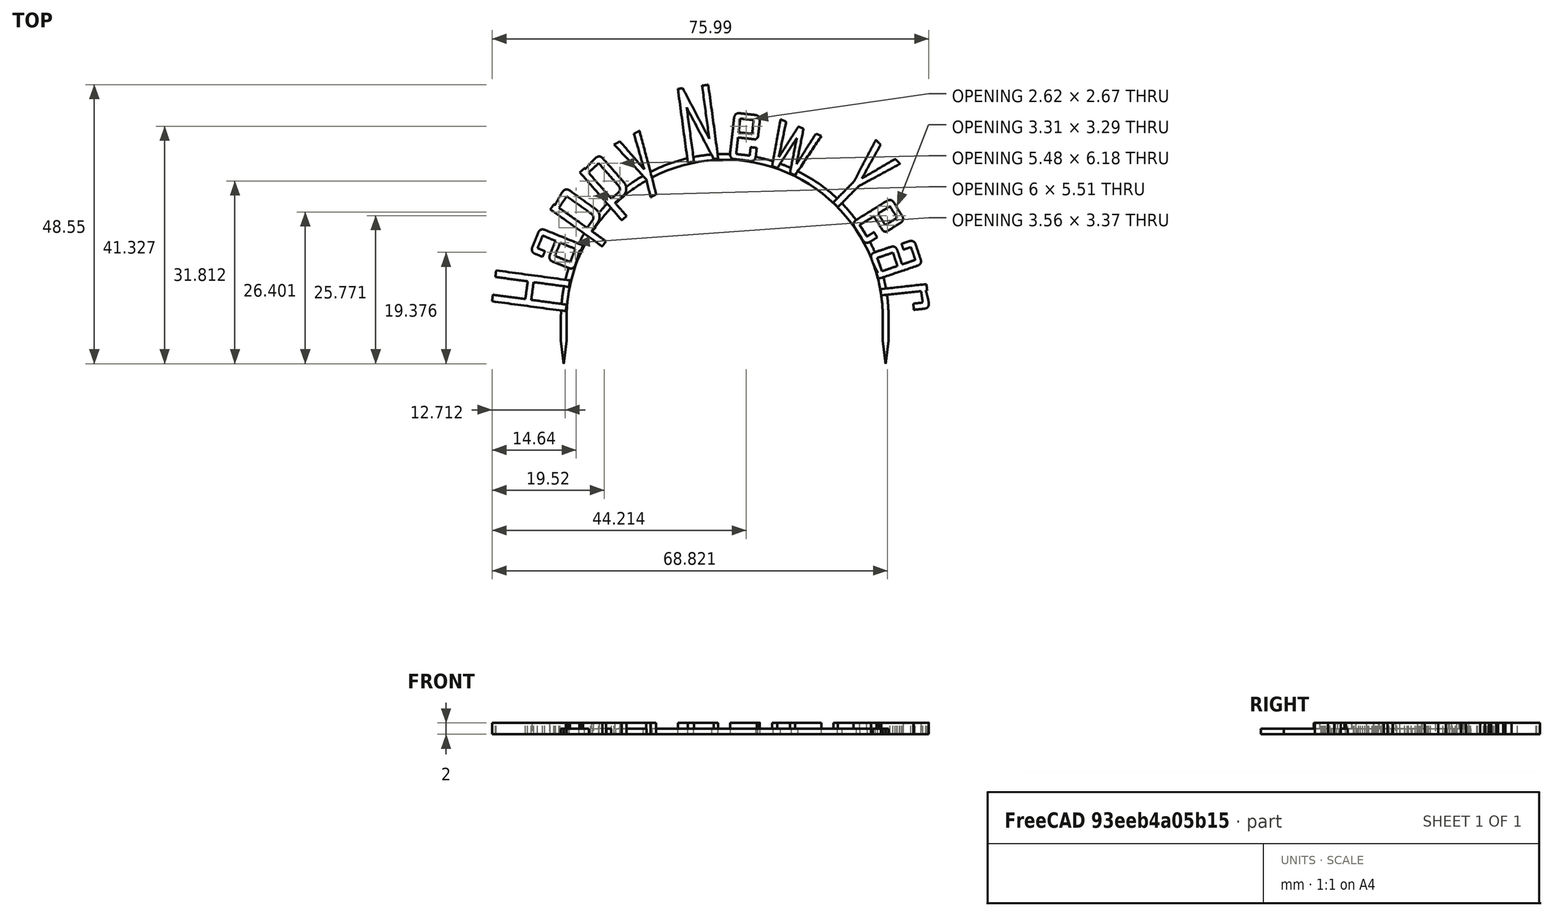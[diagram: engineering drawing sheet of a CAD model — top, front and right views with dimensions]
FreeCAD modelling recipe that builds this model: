
FCSTD DOCUMENT  (FreeCAD 0.20R29177 (Git))
Label: cake-topper-halloween
License: All rights reserved
LicenseURL: http://en.wikipedia.org/wiki/All_rights_reserved
objects: Part::Feature×18, Sketcher::SketchObject×4, PartDesign::Pad×4, App::DocumentObjectGroup×3, App::TextDocument×1, Spreadsheet::Sheet×1, PartDesign::Plane×1, PartDesign::Body×1, Mesh::Feature×1
note: 32 computed .brp shape members not serialized (recipe doc carries the construction recipe); baked Part::Feature solids carry a one-line shape summary decoded from their .brp

FEATURE [App::TextDocument] Text_document  label="Text document"
FEATURE [Spreadsheet::Sheet] Spreadsheet
  cells = A1=Text height; B1=text_h; C1(dim_text_h)==2mm; A2=Text offset x; B2=text_x; C2(dim_text_x)==-105.3mm; A3=Text offset y; B3=text_y; C3(dim_text_y)==177.4mm; A4=Scaffold height; B4=scaffold_h; C4(dim_scaffold_h)==1mm; A5=Scaffold width; B5=scaffold_w; C5(dim_scaffold_w)==1mm; A6=Scaffold inner radius; B6=scaffold_ir; C6(dim_scaffold_ir)==27.5mm; A7=Scaffold outer radius; B7=scaffold_or; C7(dim_scaffold_or)==dim_scaffold_ir + dim_scaffold_w; A8=Tines length; B8=tine_l; C8(dim_tine_l)==4mm; A9=Tines shaft length; B9=tine_shaft_l; C9(dim_tine_shaft_l)==4mm
FEATURE [PartDesign::Plane] DatumPlane  label="BaseXYDatumPlane"
  Length = 90.097
  MapMode = 5
  ResizeMode = 0
  Support = -> [XY_Plane]
  Width = 79.6672
FEATURE [Sketcher::SketchObject] Sketch001  label="ArcSketch"
  FullyConstrained = true
  MapMode = 5
  Support = -> [DatumPlane]
  expr: Constraints[15] = Spreadsheet.dim_scaffold_or
  expr: Constraints[37] = Spreadsheet.dim_tine_shaft_l
  expr: Constraints[38] = Spreadsheet.dim_tine_l
  expr: Constraints[59] = Spreadsheet.dim_scaffold_or
  expr: Constraints[6] = Spreadsheet.dim_scaffold_ir
  sketch-geometry (35):
    g0: ArcOfCircle CenterX=0 CenterY=0 CenterZ=0 NormalX=0 NormalY=0 NormalZ=1 AngleXU=0 Radius=27.5 StartAngle=0 EndAngle=3.14159
    g1: LineSegment StartX=-28.5 StartY=0 StartZ=0 EndX=-27.5 EndY=3.4e-15 EndZ=0
    g2: LineSegment StartX=27.5 StartY=0 StartZ=0 EndX=28.5 EndY=0 EndZ=0
    g3: ArcOfCircle CenterX=0 CenterY=0 CenterZ=0 NormalX=0 NormalY=0 NormalZ=1 AngleXU=0 Radius=28.5 StartAngle=0 EndAngle=0.185163
    g4: ArcOfCircle CenterX=0 CenterY=0 CenterZ=0 NormalX=0 NormalY=0 NormalZ=1 AngleXU=0 Radius=28.5 StartAngle=0.185163 EndAngle=0.207269
    g5: LineSegment StartX=27.89 StartY=5.86497 StartZ=0 EndX=33.2988 EndY=6.91633 EndZ=0
    g6: LineSegment StartX=28.0128 StartY=5.24706 StartZ=0 EndX=33.419 EndY=6.2979 EndZ=0
    g7: LineSegment StartX=33.2988 StartY=6.91633 StartZ=0 EndX=33.419 EndY=6.2979 EndZ=0
    g8: LineSegment StartX=-28.5 StartY=0 StartZ=0 EndX=-28.5 EndY=-4 EndZ=0
    g9: LineSegment StartX=-27.5 StartY=3.4e-15 StartZ=0 EndX=-27.5 EndY=-4 EndZ=0
    g10: LineSegment StartX=-28.5 StartY=-4 StartZ=0 EndX=-28 EndY=-8 EndZ=0
    g11: LineSegment StartX=-27.5 StartY=-4 StartZ=0 EndX=-28 EndY=-8 EndZ=0
    g12: LineSegment StartX=-28.5 StartY=-4 StartZ=0 EndX=-28 EndY=-4 EndZ=0
    g13: LineSegment StartX=-28 StartY=-4 StartZ=0 EndX=-27.5 EndY=-4 EndZ=0
    g14: LineSegment StartX=-28 StartY=-4 StartZ=0 EndX=-28 EndY=-8 EndZ=0
    g15: LineSegment StartX=27.5 StartY=-4 StartZ=0 EndX=28 EndY=-4 EndZ=0
    g16: LineSegment StartX=28 StartY=-4 StartZ=0 EndX=28.5 EndY=-4 EndZ=0
    g17: LineSegment StartX=28 StartY=-4 StartZ=0 EndX=28 EndY=-8 EndZ=0
    g18: LineSegment StartX=27.5 StartY=0 StartZ=0 EndX=27.5 EndY=-4 EndZ=0
    g19: LineSegment StartX=28.5 StartY=0 StartZ=0 EndX=28.5 EndY=-4 EndZ=0
    g20: LineSegment StartX=27.5 StartY=-4 StartZ=0 EndX=28 EndY=-8 EndZ=0
    g21: LineSegment StartX=28.5 StartY=-4 StartZ=0 EndX=28 EndY=-8 EndZ=0
    g22: LineSegment StartX=28.5 StartY=0 StartZ=0 EndX=28.5 EndY=28.5 EndZ=0
    g23: LineSegment StartX=27.89 StartY=5.86497 StartZ=0 EndX=0 EndY=5.86497 EndZ=0
    g24: ArcOfCircle CenterX=0 CenterY=0 CenterZ=0 NormalX=0 NormalY=0 NormalZ=1 AngleXU=0 Radius=28.5 StartAngle=2.19288 EndAngle=3.14159
    g25: ArcOfCircle CenterX=0 CenterY=0 CenterZ=0 NormalX=0 NormalY=0 NormalZ=1 AngleXU=0 Radius=28.5 StartAngle=0.207269 EndAngle=2.17112
    g26: ArcOfCircle CenterX=0 CenterY=0 CenterZ=0 NormalX=0 NormalY=0 NormalZ=1 AngleXU=0 Radius=28.5 StartAngle=2.17112 EndAngle=2.19288
    g27: LineSegment StartX=-16.6078 StartY=23.161 StartZ=0 EndX=-19.8518 EndY=27.7734 EndZ=0
    g28: LineSegment StartX=-16.1 StartY=23.5168 StartZ=0 EndX=-19.3446 EndY=28.13 EndZ=0
    g29: LineSegment StartX=-19.8518 StartY=27.7734 StartZ=0 EndX=-19.3446 EndY=28.13 EndZ=0
    g30: LineSegment StartX=-16.1 StartY=23.5168 StartZ=0 EndX=0 EndY=23.5168 EndZ=0
    g31: LineSegment StartX=28.5 StartY=28.5 StartZ=0 EndX=0 EndY=28.5 EndZ=0
    g32: LineSegment StartX=0 StartY=28.5 StartZ=0 EndX=-28.5 EndY=28.5 EndZ=0
    g33: LineSegment StartX=-28.5 StartY=0 StartZ=0 EndX=-28.5 EndY=28.5 EndZ=0
    g34: LineSegment StartX=-19.8518 StartY=28.5 StartZ=0 EndX=-19.8518 EndY=27.7734 EndZ=0
  constraints (96):
    c: Coincident(g0,g-1)
    c: PointOnObject(g0,g-1)
    c: PointOnObject(g0,g-1)
    c: Coincident(g3,g0)
    c: PointOnObject(g24,g-1)
    c: PointOnObject(g3,g-1)
    c: Radius(g0) = 27.5
    c: Coincident(g1,g24)
    c: Coincident(g1,g0)
    c: Coincident(g2,g0)
    c: Coincident(g2,g3)
    c: Coincident(g4,g25)
    c: Coincident(g3,g25)
    c: Coincident(g3,g4)
    c: Coincident(g3,g4)
    c: Radius(g3) = 28.5
    c: Coincident(g5,g25)
    c: Coincident(g6,g3)
    c: Coincident(g7,g5)
    c: Parallel(g5,g6)
    c: Perpendicular(g7,g5)
    c: Coincident(g8,g24)
    c: Vertical(g8)
    c: Coincident(g9,g0)
    c: Vertical(g9)
    c: Coincident(g10,g8)
    c: Coincident(g11,g9)
    c: Coincident(g11,g10)
    c: Coincident(g12,g8)
    c: Horizontal(g12)
    c: Coincident(g13,g12)
    c: Coincident(g13,g9)
    c: Horizontal(g13)
    c: Coincident(g14,g12)
    c: Coincident(g14,g10)
    c: Equal(g13,g12)
    c: Vertical(g14)
    c: DistanceY(g9,g9) = 4
    c: DistanceY(g10,g9) = 4
    c: Horizontal(g15)
    c: Coincident(g16,g15)
    c: Horizontal(g16)
    c: Coincident(g17,g15)
    c: Vertical(g17)
    c: Coincident(g18,g0)
    c: Coincident(g18,g15)
    c: Vertical(g18)
    c: Coincident(g19,g3)
    c: Coincident(g19,g16)
    c: Vertical(g19)
    c: Coincident(g20,g18)
    c: Coincident(g20,g17)
    c: Coincident(g21,g19)
    c: Coincident(g21,g20)
    c: Equal(g18,g9)
    c: Equal(g17,g14)
    c: Equal(g16,g15)
    c: Coincident(g22,g3)
    c: Vertical(g22)
    c: DistanceY(g22,g22) = 28.5
    c: Coincident(g7,g6)
    c: Coincident(g23,g25)
    c: PointOnObject(g23,g-2)
    c: Horizontal(g23)
    c: DistanceX(g23,g23) = 27.89
    c: Distance(g5) = 5.51
    c: Distance(g7) = 0.63
    c: Angle(g5,g22) = 1.37881
    c: Coincident(g26,g24)
    c: Coincident(g25,g24)
    c: Coincident(g25,g26)
    c: Coincident(g25,g26)
    c: Coincident(g27,g24)
    c: Coincident(g28,g25)
    c: Coincident(g29,g27)
    c: Coincident(g29,g28)
    c: Perpendicular(g27,g29)
    c: Distance(g29) = 0.62
    c: Perpendicular(g28,g29)
    c: Coincident(g30,g25)
    c: PointOnObject(g30,g-2)
    c: Horizontal(g30)
    c: DistanceX(g30,g30) = 16.1
    c: Coincident(g31,g22)
    c: PointOnObject(g31,g-2)
    c: Horizontal(g31)
    c: Coincident(g32,g31)
    c: Horizontal(g32)
    c: Coincident(g33,g8)
    c: Coincident(g33,g32)
    c: Vertical(g33)
    c: PointOnObject(g34,g32)
    c: Coincident(g34,g27)
    c: Vertical(g34)
    c: Angle(g29,g34) = 0.957837
    c: Distance(g28) = 5.64
FEATURE [PartDesign::Pad] Pad  label="ArcPad"
  Direction = (0,0,1)
  Length = 1
  Length2 = 10
  Profile = -> Sketch001
  ReferenceAxis = -> Sketch001 [N_Axis]
  Type = 0
  expr: Length = Spreadsheet.dim_scaffold_h
FEATURE [Part::Feature] path43751
  shape: bbox 13.55 x 7.097 x 2e-07 mm, 0 faces, 0 solids (baked)
FEATURE [Part::Feature] path43753
  shape: bbox 9.02 x 7.052 x 2e-07 mm, 0 faces, 0 solids (baked)
FEATURE [Part::Feature] path43753001
  shape: bbox 3.56 x 3.366 x 2e-07 mm, 0 faces, 0 solids (baked)
FEATURE [Part::Feature] path43755
  shape: bbox 9.677 x 10.03 x 2e-07 mm, 0 faces, 0 solids (baked)
FEATURE [Part::Feature] path43755001
  shape: bbox 6.117 x 5.508 x 2e-07 mm, 0 faces, 0 solids (baked)
FEATURE [Part::Feature] path43757
  shape: bbox 8.151 x 11.22 x 2e-07 mm, 0 faces, 0 solids (baked)
FEATURE [Part::Feature] path43757001
  shape: bbox 5.598 x 6.176 x 2e-07 mm, 0 faces, 0 solids (baked)
FEATURE [Part::Feature] path43759
  shape: bbox 7.288 x 11.57 x 2e-07 mm, 0 faces, 0 solids (baked)
FEATURE [App::DocumentObjectGroup] Group  label="HappyGroup"
  Group = -> [path43751,path43753,path43753001,path43755,path43755001,path43757,path43757001,path43759]
FEATURE [Part::Feature] path43761
  shape: bbox 7.025 x 13.54 x 2e-07 mm, 0 faces, 0 solids (baked)
FEATURE [Part::Feature] path43763
  shape: bbox 5.373 x 8.499 x 2e-07 mm, 0 faces, 0 solids (baked)
FEATURE [Part::Feature] path43763001
  shape: bbox 2.622 x 2.673 x 2e-07 mm, 0 faces, 0 solids (baked)
FEATURE [Part::Feature] path43765
  shape: bbox 8.563 x 9.714 x 2e-07 mm, 0 faces, 0 solids (baked)
FEATURE [App::DocumentObjectGroup] Group001  label="NewGroup"
  Group = -> [path43761,path43763,path43763001,path43765]
FEATURE [Part::Feature] path43767
  shape: bbox 11.59 x 11.67 x 2e-07 mm, 0 faces, 0 solids (baked)
FEATURE [Part::Feature] path43769
  shape: bbox 8.812 x 7.677 x 2e-07 mm, 0 faces, 0 solids (baked)
FEATURE [Part::Feature] path43769001
  shape: bbox 3.306 x 3.288 x 2e-07 mm, 0 faces, 0 solids (baked)
FEATURE [Part::Feature] path43771
  shape: bbox 8.942 x 6.735 x 2e-07 mm, 0 faces, 0 solids (baked)
FEATURE [Part::Feature] path43771001
  shape: bbox 3.527 x 3.236 x 2e-07 mm, 0 faces, 0 solids (baked)
FEATURE [Part::Feature] path43773
  shape: bbox 8.499 x 4.468 x 2e-07 mm, 0 faces, 0 solids (baked)
FEATURE [App::DocumentObjectGroup] Group002  label="YearGroup"
  Group = -> [path43767,path43769,path43769001,path43771,path43771001,path43773]
FEATURE [Sketcher::SketchObject] Sketch002  label="HappySketch"
  FullyConstrained = false
  Placement = pos=(-105.3,177.4,0) rot=(0,0,1;0rad)
  expr: .Placement.Base.x = Spreadsheet.dim_text_x
  expr: .Placement.Base.y = Spreadsheet.dim_text_y
  sketch-geometry (77):
    g0: BSplineCurve PolesCount=2 KnotsCount=2 Degree=1 IsPeriodic=0
    g1: BSplineCurve PolesCount=2 KnotsCount=2 Degree=1 IsPeriodic=0
    g2: BSplineCurve PolesCount=2 KnotsCount=2 Degree=1 IsPeriodic=0
    g3: BSplineCurve PolesCount=2 KnotsCount=2 Degree=1 IsPeriodic=0
    g4: BSplineCurve PolesCount=2 KnotsCount=2 Degree=1 IsPeriodic=0
    g5: BSplineCurve PolesCount=2 KnotsCount=2 Degree=1 IsPeriodic=0
    g6: BSplineCurve PolesCount=2 KnotsCount=2 Degree=1 IsPeriodic=0
    g7: BSplineCurve PolesCount=2 KnotsCount=2 Degree=1 IsPeriodic=0
    g8: BSplineCurve PolesCount=2 KnotsCount=2 Degree=1 IsPeriodic=0
    g9: BSplineCurve PolesCount=2 KnotsCount=2 Degree=1 IsPeriodic=0
    g10: BSplineCurve PolesCount=2 KnotsCount=2 Degree=1 IsPeriodic=0
    g11: BSplineCurve PolesCount=2 KnotsCount=2 Degree=1 IsPeriodic=0
    g12: BSplineCurve PolesCount=2 KnotsCount=2 Degree=1 IsPeriodic=0
    g13: BSplineCurve PolesCount=2 KnotsCount=2 Degree=1 IsPeriodic=0
    g14: BSplineCurve PolesCount=3 KnotsCount=2 Degree=2 IsPeriodic=0
    g15: BSplineCurve PolesCount=3 KnotsCount=2 Degree=2 IsPeriodic=0
    g16: BSplineCurve PolesCount=3 KnotsCount=2 Degree=2 IsPeriodic=0
    g17: BSplineCurve PolesCount=2 KnotsCount=2 Degree=1 IsPeriodic=0
    g18: BSplineCurve PolesCount=3 KnotsCount=2 Degree=2 IsPeriodic=0
    g19: BSplineCurve PolesCount=2 KnotsCount=2 Degree=1 IsPeriodic=0
    g20: BSplineCurve PolesCount=2 KnotsCount=2 Degree=1 IsPeriodic=0
    g21: BSplineCurve PolesCount=2 KnotsCount=2 Degree=1 IsPeriodic=0
    g22: BSplineCurve PolesCount=2 KnotsCount=2 Degree=1 IsPeriodic=0
    g23: BSplineCurve PolesCount=2 KnotsCount=2 Degree=1 IsPeriodic=0
    g24: BSplineCurve PolesCount=2 KnotsCount=2 Degree=1 IsPeriodic=0
    g25: BSplineCurve PolesCount=3 KnotsCount=2 Degree=2 IsPeriodic=0
    g26: BSplineCurve PolesCount=2 KnotsCount=2 Degree=1 IsPeriodic=0
    g27: BSplineCurve PolesCount=3 KnotsCount=2 Degree=2 IsPeriodic=0
    g28: BSplineCurve PolesCount=2 KnotsCount=2 Degree=1 IsPeriodic=0
    g29: BSplineCurve PolesCount=2 KnotsCount=2 Degree=1 IsPeriodic=0
    g30: BSplineCurve PolesCount=2 KnotsCount=2 Degree=1 IsPeriodic=0
    g31: BSplineCurve PolesCount=2 KnotsCount=2 Degree=1 IsPeriodic=0
    g32: BSplineCurve PolesCount=2 KnotsCount=2 Degree=1 IsPeriodic=0
    g33: BSplineCurve PolesCount=3 KnotsCount=2 Degree=2 IsPeriodic=0
    g34: BSplineCurve PolesCount=3 KnotsCount=2 Degree=2 IsPeriodic=0
    g35: BSplineCurve PolesCount=2 KnotsCount=2 Degree=1 IsPeriodic=0
    g36: BSplineCurve PolesCount=2 KnotsCount=2 Degree=1 IsPeriodic=0
    g37: BSplineCurve PolesCount=2 KnotsCount=2 Degree=1 IsPeriodic=0
    g38: BSplineCurve PolesCount=2 KnotsCount=2 Degree=1 IsPeriodic=0
    g39: BSplineCurve PolesCount=2 KnotsCount=2 Degree=1 IsPeriodic=0
    g40: BSplineCurve PolesCount=2 KnotsCount=2 Degree=1 IsPeriodic=0
    g41: BSplineCurve PolesCount=3 KnotsCount=2 Degree=2 IsPeriodic=0
    g42: BSplineCurve PolesCount=3 KnotsCount=2 Degree=2 IsPeriodic=0
    g43: BSplineCurve PolesCount=3 KnotsCount=2 Degree=2 IsPeriodic=0
    g44: BSplineCurve PolesCount=2 KnotsCount=2 Degree=1 IsPeriodic=0
    g45: BSplineCurve PolesCount=2 KnotsCount=2 Degree=1 IsPeriodic=0
    g46: BSplineCurve PolesCount=2 KnotsCount=2 Degree=1 IsPeriodic=0
    g47: BSplineCurve PolesCount=2 KnotsCount=2 Degree=1 IsPeriodic=0
    g48: BSplineCurve PolesCount=2 KnotsCount=2 Degree=1 IsPeriodic=0
    g49: BSplineCurve PolesCount=3 KnotsCount=2 Degree=2 IsPeriodic=0
    g50: BSplineCurve PolesCount=2 KnotsCount=2 Degree=1 IsPeriodic=0
    g51: BSplineCurve PolesCount=3 KnotsCount=2 Degree=2 IsPeriodic=0
    g52: BSplineCurve PolesCount=3 KnotsCount=2 Degree=2 IsPeriodic=0
    g53: BSplineCurve PolesCount=2 KnotsCount=2 Degree=1 IsPeriodic=0
    g54: BSplineCurve PolesCount=2 KnotsCount=2 Degree=1 IsPeriodic=0
    g55: BSplineCurve PolesCount=2 KnotsCount=2 Degree=1 IsPeriodic=0
    g56: BSplineCurve PolesCount=2 KnotsCount=2 Degree=1 IsPeriodic=0
    g57: BSplineCurve PolesCount=2 KnotsCount=2 Degree=1 IsPeriodic=0
    g58: BSplineCurve PolesCount=2 KnotsCount=2 Degree=1 IsPeriodic=0
    g59: BSplineCurve PolesCount=3 KnotsCount=2 Degree=2 IsPeriodic=0
    g60: BSplineCurve PolesCount=3 KnotsCount=2 Degree=2 IsPeriodic=0
    g61: BSplineCurve PolesCount=3 KnotsCount=2 Degree=2 IsPeriodic=0
    g62: BSplineCurve PolesCount=2 KnotsCount=2 Degree=1 IsPeriodic=0
    g63: BSplineCurve PolesCount=2 KnotsCount=2 Degree=1 IsPeriodic=0
    g64: BSplineCurve PolesCount=2 KnotsCount=2 Degree=1 IsPeriodic=0
    g65: BSplineCurve PolesCount=2 KnotsCount=2 Degree=1 IsPeriodic=0
    g66: BSplineCurve PolesCount=2 KnotsCount=2 Degree=1 IsPeriodic=0
    g67: BSplineCurve PolesCount=3 KnotsCount=2 Degree=2 IsPeriodic=0
    g68: BSplineCurve PolesCount=2 KnotsCount=2 Degree=1 IsPeriodic=0
    g69: BSplineCurve PolesCount=2 KnotsCount=2 Degree=1 IsPeriodic=0
    g70: BSplineCurve PolesCount=2 KnotsCount=2 Degree=1 IsPeriodic=0
    g71: BSplineCurve PolesCount=2 KnotsCount=2 Degree=1 IsPeriodic=0
    g72: BSplineCurve PolesCount=2 KnotsCount=2 Degree=1 IsPeriodic=0
    g73: BSplineCurve PolesCount=2 KnotsCount=2 Degree=1 IsPeriodic=0
    g74: BSplineCurve PolesCount=2 KnotsCount=2 Degree=1 IsPeriodic=0
    g75: BSplineCurve PolesCount=2 KnotsCount=2 Degree=1 IsPeriodic=0
    g76: BSplineCurve PolesCount=2 KnotsCount=2 Degree=1 IsPeriodic=0
  constraints (77):
    c: Coincident(g0,g1)
    c: Coincident(g1,g2)
    c: Coincident(g2,g3)
    c: Coincident(g3,g4)
    c: Coincident(g4,g5)
    c: Coincident(g5,g6)
    c: Coincident(g6,g7)
    c: Coincident(g7,g8)
    c: Coincident(g8,g9)
    c: Coincident(g9,g10)
    c: Coincident(g10,g11)
    c: Coincident(g11,g0)
    c: Coincident(g12,g13)
    c: Coincident(g13,g14)
    c: Coincident(g14,g15)
    c: Coincident(g15,g16)
    c: Coincident(g16,g17)
    c: Coincident(g17,g18)
    c: Coincident(g18,g19)
    c: Coincident(g19,g20)
    c: Coincident(g20,g21)
    c: Coincident(g21,g22)
    c: Coincident(g22,g23)
    c: Coincident(g23,g24)
    c: Coincident(g24,g25)
    c: Coincident(g25,g26)
    c: Coincident(g26,g27)
    c: Coincident(g27,g28)
    c: Coincident(g28,g12)
    c: Coincident(g29,g30)
    c: Coincident(g30,g31)
    c: Coincident(g31,g32)
    c: Coincident(g32,g29)
    c: Coincident(g33,g34)
    c: Coincident(g34,g35)
    c: Coincident(g35,g36)
    c: Coincident(g36,g37)
    c: Coincident(g37,g38)
    c: Coincident(g38,g39)
    c: Coincident(g39,g40)
    c: Coincident(g40,g41)
    c: Coincident(g41,g42)
    c: Coincident(g42,g43)
    c: Coincident(g43,g44)
    c: Coincident(g44,g33)
    c: Coincident(g45,g46)
    c: Coincident(g46,g47)
    c: Coincident(g47,g48)
    c: Coincident(g48,g49)
    c: Coincident(g49,g50)
    c: Coincident(g50,g45)
    c: Coincident(g51,g52)
    c: Coincident(g52,g53)
    c: Coincident(g53,g54)
    c: Coincident(g54,g55)
    c: Coincident(g55,g56)
    c: Coincident(g56,g57)
    c: Coincident(g57,g58)
    c: Coincident(g58,g59)
    c: Coincident(g59,g60)
    c: Coincident(g60,g61)
    c: Coincident(g61,g62)
    c: Coincident(g62,g51)
    c: Coincident(g63,g64)
    c: Coincident(g64,g65)
    c: Coincident(g65,g66)
    c: Coincident(g66,g67)
    c: Coincident(g67,g63)
    c: Coincident(g68,g69)
    c: Coincident(g69,g70)
    c: Coincident(g70,g71)
    c: Coincident(g71,g72)
    c: Coincident(g72,g73)
    c: Coincident(g73,g74)
    c: Coincident(g74,g75)
    c: Coincident(g75,g76)
    c: Coincident(g76,g68)
FEATURE [Sketcher::SketchObject] Sketch003  label="NewSketch"
  FullyConstrained = false
  Placement = pos=(-105.3,177.4,0) rot=(0,0,1;0rad)
  expr: .Placement.Base.x = Spreadsheet.dim_text_x
  expr: .Placement.Base.y = Spreadsheet.dim_text_y
  sketch-geometry (42):
    g0: BSplineCurve PolesCount=2 KnotsCount=2 Degree=1 IsPeriodic=0
    g1: BSplineCurve PolesCount=2 KnotsCount=2 Degree=1 IsPeriodic=0
    g2: BSplineCurve PolesCount=2 KnotsCount=2 Degree=1 IsPeriodic=0
    g3: BSplineCurve PolesCount=2 KnotsCount=2 Degree=1 IsPeriodic=0
    g4: BSplineCurve PolesCount=2 KnotsCount=2 Degree=1 IsPeriodic=0
    g5: BSplineCurve PolesCount=2 KnotsCount=2 Degree=1 IsPeriodic=0
    g6: BSplineCurve PolesCount=2 KnotsCount=2 Degree=1 IsPeriodic=0
    g7: BSplineCurve PolesCount=2 KnotsCount=2 Degree=1 IsPeriodic=0
    g8: BSplineCurve PolesCount=2 KnotsCount=2 Degree=1 IsPeriodic=0
    g9: BSplineCurve PolesCount=2 KnotsCount=2 Degree=1 IsPeriodic=0
    g10: BSplineCurve PolesCount=3 KnotsCount=2 Degree=2 IsPeriodic=0
    g11: BSplineCurve PolesCount=2 KnotsCount=2 Degree=1 IsPeriodic=0
    g12: BSplineCurve PolesCount=3 KnotsCount=2 Degree=2 IsPeriodic=0
    g13: BSplineCurve PolesCount=2 KnotsCount=2 Degree=1 IsPeriodic=0
    g14: BSplineCurve PolesCount=3 KnotsCount=2 Degree=2 IsPeriodic=0
    g15: BSplineCurve PolesCount=2 KnotsCount=2 Degree=1 IsPeriodic=0
    g16: BSplineCurve PolesCount=3 KnotsCount=2 Degree=2 IsPeriodic=0
    g17: BSplineCurve PolesCount=2 KnotsCount=2 Degree=1 IsPeriodic=0
    g18: BSplineCurve PolesCount=2 KnotsCount=2 Degree=1 IsPeriodic=0
    g19: BSplineCurve PolesCount=2 KnotsCount=2 Degree=1 IsPeriodic=0
    g20: BSplineCurve PolesCount=2 KnotsCount=2 Degree=1 IsPeriodic=0
    g21: BSplineCurve PolesCount=2 KnotsCount=2 Degree=1 IsPeriodic=0
    g22: BSplineCurve PolesCount=2 KnotsCount=2 Degree=1 IsPeriodic=0
    g23: BSplineCurve PolesCount=2 KnotsCount=2 Degree=1 IsPeriodic=0
    g24: BSplineCurve PolesCount=2 KnotsCount=2 Degree=1 IsPeriodic=0
    g25: BSplineCurve PolesCount=2 KnotsCount=2 Degree=1 IsPeriodic=0
    g26: BSplineCurve PolesCount=2 KnotsCount=2 Degree=1 IsPeriodic=0
    g27: BSplineCurve PolesCount=2 KnotsCount=2 Degree=1 IsPeriodic=0
    g28: BSplineCurve PolesCount=2 KnotsCount=2 Degree=1 IsPeriodic=0
    g29: BSplineCurve PolesCount=2 KnotsCount=2 Degree=1 IsPeriodic=0
    g30: BSplineCurve PolesCount=2 KnotsCount=2 Degree=1 IsPeriodic=0
    g31: BSplineCurve PolesCount=2 KnotsCount=2 Degree=1 IsPeriodic=0
    g32: BSplineCurve PolesCount=2 KnotsCount=2 Degree=1 IsPeriodic=0
    g33: BSplineCurve PolesCount=2 KnotsCount=2 Degree=1 IsPeriodic=0
    g34: BSplineCurve PolesCount=2 KnotsCount=2 Degree=1 IsPeriodic=0
    g35: BSplineCurve PolesCount=2 KnotsCount=2 Degree=1 IsPeriodic=0
    g36: BSplineCurve PolesCount=2 KnotsCount=2 Degree=1 IsPeriodic=0
    g37: BSplineCurve PolesCount=2 KnotsCount=2 Degree=1 IsPeriodic=0
    g38: BSplineCurve PolesCount=2 KnotsCount=2 Degree=1 IsPeriodic=0
    g39: BSplineCurve PolesCount=2 KnotsCount=2 Degree=1 IsPeriodic=0
    g40: BSplineCurve PolesCount=2 KnotsCount=2 Degree=1 IsPeriodic=0
    g41: BSplineCurve PolesCount=2 KnotsCount=2 Degree=1 IsPeriodic=0
  constraints (42):
    c: Coincident(g0,g1)
    c: Coincident(g1,g2)
    c: Coincident(g2,g3)
    c: Coincident(g3,g4)
    c: Coincident(g4,g5)
    c: Coincident(g5,g6)
    c: Coincident(g6,g7)
    c: Coincident(g7,g8)
    c: Coincident(g8,g9)
    c: Coincident(g9,g0)
    c: Coincident(g10,g11)
    c: Coincident(g11,g12)
    c: Coincident(g12,g13)
    c: Coincident(g13,g14)
    c: Coincident(g14,g15)
    c: Coincident(g15,g16)
    c: Coincident(g16,g17)
    c: Coincident(g17,g18)
    c: Coincident(g18,g19)
    c: Coincident(g19,g20)
    c: Coincident(g20,g21)
    c: Coincident(g21,g22)
    c: Coincident(g22,g23)
    c: Coincident(g23,g24)
    c: Coincident(g24,g10)
    c: Coincident(g25,g26)
    c: Coincident(g26,g27)
    c: Coincident(g27,g28)
    c: Coincident(g28,g25)
    c: Coincident(g29,g30)
    c: Coincident(g30,g31)
    c: Coincident(g31,g32)
    c: Coincident(g32,g33)
    c: Coincident(g33,g34)
    c: Coincident(g34,g35)
    c: Coincident(g35,g36)
    c: Coincident(g36,g37)
    c: Coincident(g37,g38)
    c: Coincident(g38,g39)
    c: Coincident(g39,g40)
    c: Coincident(g40,g41)
    c: Coincident(g41,g29)
FEATURE [Sketcher::SketchObject] Sketch004  label="YearSketch"
  FullyConstrained = false
  Placement = pos=(-105.3,177.4,0) rot=(0,0,1;0rad)
  expr: .Placement.Base.x = Spreadsheet.dim_text_x
  expr: .Placement.Base.y = Spreadsheet.dim_text_y
  sketch-geometry (66):
    g0: BSplineCurve PolesCount=2 KnotsCount=2 Degree=1 IsPeriodic=0
    g1: BSplineCurve PolesCount=3 KnotsCount=2 Degree=2 IsPeriodic=0
    g2: BSplineCurve PolesCount=2 KnotsCount=2 Degree=1 IsPeriodic=0
    g3: BSplineCurve PolesCount=2 KnotsCount=2 Degree=1 IsPeriodic=0
    g4: BSplineCurve PolesCount=2 KnotsCount=2 Degree=1 IsPeriodic=0
    g5: BSplineCurve PolesCount=3 KnotsCount=2 Degree=2 IsPeriodic=0
    g6: BSplineCurve PolesCount=3 KnotsCount=2 Degree=2 IsPeriodic=0
    g7: BSplineCurve PolesCount=2 KnotsCount=2 Degree=1 IsPeriodic=0
    g8: BSplineCurve PolesCount=3 KnotsCount=2 Degree=2 IsPeriodic=0
    g9: BSplineCurve PolesCount=2 KnotsCount=2 Degree=1 IsPeriodic=0
    g10: BSplineCurve PolesCount=2 KnotsCount=2 Degree=1 IsPeriodic=0
    g11: BSplineCurve PolesCount=2 KnotsCount=2 Degree=1 IsPeriodic=0
    g12: BSplineCurve PolesCount=2 KnotsCount=2 Degree=1 IsPeriodic=0
    g13: BSplineCurve PolesCount=3 KnotsCount=2 Degree=2 IsPeriodic=0
    g14: BSplineCurve PolesCount=3 KnotsCount=2 Degree=2 IsPeriodic=0
    g15: BSplineCurve PolesCount=2 KnotsCount=2 Degree=1 IsPeriodic=0
    g16: BSplineCurve PolesCount=3 KnotsCount=2 Degree=2 IsPeriodic=0
    g17: BSplineCurve PolesCount=2 KnotsCount=2 Degree=1 IsPeriodic=0
    g18: BSplineCurve PolesCount=3 KnotsCount=2 Degree=2 IsPeriodic=0
    g19: BSplineCurve PolesCount=2 KnotsCount=2 Degree=1 IsPeriodic=0
    g20: BSplineCurve PolesCount=3 KnotsCount=2 Degree=2 IsPeriodic=0
    g21: BSplineCurve PolesCount=2 KnotsCount=2 Degree=1 IsPeriodic=0
    g22: BSplineCurve PolesCount=2 KnotsCount=2 Degree=1 IsPeriodic=0
    g23: BSplineCurve PolesCount=2 KnotsCount=2 Degree=1 IsPeriodic=0
    g24: BSplineCurve PolesCount=2 KnotsCount=2 Degree=1 IsPeriodic=0
    g25: BSplineCurve PolesCount=2 KnotsCount=2 Degree=1 IsPeriodic=0
    g26: BSplineCurve PolesCount=2 KnotsCount=2 Degree=1 IsPeriodic=0
    g27: BSplineCurve PolesCount=2 KnotsCount=2 Degree=1 IsPeriodic=0
    g28: BSplineCurve PolesCount=2 KnotsCount=2 Degree=1 IsPeriodic=0
    g29: BSplineCurve PolesCount=2 KnotsCount=2 Degree=1 IsPeriodic=0
    g30: BSplineCurve PolesCount=2 KnotsCount=2 Degree=1 IsPeriodic=0
    g31: BSplineCurve PolesCount=2 KnotsCount=2 Degree=1 IsPeriodic=0
    g32: BSplineCurve PolesCount=2 KnotsCount=2 Degree=1 IsPeriodic=0
    g33: BSplineCurve PolesCount=2 KnotsCount=2 Degree=1 IsPeriodic=0
    g34: BSplineCurve PolesCount=2 KnotsCount=2 Degree=1 IsPeriodic=0
    g35: BSplineCurve PolesCount=3 KnotsCount=2 Degree=2 IsPeriodic=0
    g36: BSplineCurve PolesCount=3 KnotsCount=2 Degree=2 IsPeriodic=0
    g37: BSplineCurve PolesCount=3 KnotsCount=2 Degree=2 IsPeriodic=0
    g38: BSplineCurve PolesCount=2 KnotsCount=2 Degree=1 IsPeriodic=0
    g39: BSplineCurve PolesCount=3 KnotsCount=2 Degree=2 IsPeriodic=0
    g40: BSplineCurve PolesCount=2 KnotsCount=2 Degree=1 IsPeriodic=0
    g41: BSplineCurve PolesCount=2 KnotsCount=2 Degree=1 IsPeriodic=0
    g42: BSplineCurve PolesCount=2 KnotsCount=2 Degree=1 IsPeriodic=0
    g43: BSplineCurve PolesCount=2 KnotsCount=2 Degree=1 IsPeriodic=0
    g44: BSplineCurve PolesCount=2 KnotsCount=2 Degree=1 IsPeriodic=0
    g45: BSplineCurve PolesCount=2 KnotsCount=2 Degree=1 IsPeriodic=0
    g46: BSplineCurve PolesCount=3 KnotsCount=2 Degree=2 IsPeriodic=0
    g47: BSplineCurve PolesCount=2 KnotsCount=2 Degree=1 IsPeriodic=0
    g48: BSplineCurve PolesCount=3 KnotsCount=2 Degree=2 IsPeriodic=0
    g49: BSplineCurve PolesCount=2 KnotsCount=2 Degree=1 IsPeriodic=0
    g50: BSplineCurve PolesCount=2 KnotsCount=2 Degree=1 IsPeriodic=0
    g51: BSplineCurve PolesCount=2 KnotsCount=2 Degree=1 IsPeriodic=0
    g52: BSplineCurve PolesCount=2 KnotsCount=2 Degree=1 IsPeriodic=0
    g53: BSplineCurve PolesCount=2 KnotsCount=2 Degree=1 IsPeriodic=0
    g54: BSplineCurve PolesCount=2 KnotsCount=2 Degree=1 IsPeriodic=0
    g55: BSplineCurve PolesCount=2 KnotsCount=2 Degree=1 IsPeriodic=0
    g56: BSplineCurve PolesCount=2 KnotsCount=2 Degree=1 IsPeriodic=0
    g57: BSplineCurve PolesCount=2 KnotsCount=2 Degree=1 IsPeriodic=0
    g58: BSplineCurve PolesCount=2 KnotsCount=2 Degree=1 IsPeriodic=0
    g59: BSplineCurve PolesCount=2 KnotsCount=2 Degree=1 IsPeriodic=0
    g60: BSplineCurve PolesCount=2 KnotsCount=2 Degree=1 IsPeriodic=0
    g61: BSplineCurve PolesCount=2 KnotsCount=2 Degree=1 IsPeriodic=0
    g62: BSplineCurve PolesCount=3 KnotsCount=2 Degree=2 IsPeriodic=0
    g63: BSplineCurve PolesCount=3 KnotsCount=2 Degree=2 IsPeriodic=0
    g64: BSplineCurve PolesCount=3 KnotsCount=2 Degree=2 IsPeriodic=0
    g65: BSplineCurve PolesCount=2 KnotsCount=2 Degree=1 IsPeriodic=0
  constraints (66):
    c: Coincident(g0,g1)
    c: Coincident(g1,g2)
    c: Coincident(g2,g3)
    c: Coincident(g3,g4)
    c: Coincident(g4,g5)
    c: Coincident(g5,g6)
    c: Coincident(g6,g7)
    c: Coincident(g7,g8)
    c: Coincident(g8,g9)
    c: Coincident(g9,g10)
    c: Coincident(g10,g11)
    c: Coincident(g11,g12)
    c: Coincident(g12,g13)
    c: Coincident(g13,g0)
    c: Coincident(g14,g15)
    c: Coincident(g15,g16)
    c: Coincident(g16,g17)
    c: Coincident(g17,g18)
    c: Coincident(g18,g19)
    c: Coincident(g19,g20)
    c: Coincident(g20,g21)
    c: Coincident(g21,g22)
    c: Coincident(g22,g23)
    c: Coincident(g23,g24)
    c: Coincident(g24,g25)
    c: Coincident(g25,g26)
    c: Coincident(g26,g27)
    c: Coincident(g27,g28)
    c: Coincident(g28,g14)
    c: Coincident(g29,g30)
    c: Coincident(g30,g31)
    c: Coincident(g31,g32)
    c: Coincident(g32,g29)
    c: Coincident(g33,g34)
    c: Coincident(g34,g35)
    c: Coincident(g35,g36)
    c: Coincident(g36,g37)
    c: Coincident(g37,g38)
    c: Coincident(g38,g39)
    c: Coincident(g39,g40)
    c: Coincident(g40,g41)
    c: Coincident(g41,g42)
    c: Coincident(g42,g43)
    c: Coincident(g43,g44)
    c: Coincident(g44,g45)
    c: Coincident(g45,g46)
    c: Coincident(g46,g47)
    c: Coincident(g47,g48)
    c: Coincident(g48,g49)
    c: Coincident(g49,g33)
    c: Coincident(g50,g51)
    c: Coincident(g51,g52)
    c: Coincident(g52,g53)
    c: Coincident(g53,g50)
    c: Coincident(g54,g55)
    c: Coincident(g55,g56)
    c: Coincident(g56,g57)
    c: Coincident(g57,g58)
    c: Coincident(g58,g59)
    c: Coincident(g59,g60)
    c: Coincident(g60,g61)
    c: Coincident(g61,g62)
    c: Coincident(g62,g63)
    c: Coincident(g63,g64)
    c: Coincident(g64,g65)
    c: Coincident(g65,g54)
FEATURE [PartDesign::Pad] Pad001  label="HappyPad"
  BaseFeature = -> Pad
  Direction = (0,0,1)
  Length = 2
  Length2 = 10
  Profile = -> Sketch002
  ReferenceAxis = -> Sketch002 [N_Axis]
  Type = 0
  expr: Length = Spreadsheet.dim_text_h
FEATURE [PartDesign::Pad] Pad002  label="NewPad"
  BaseFeature = -> Pad001
  Direction = (0,0,1)
  Length = 2
  Length2 = 10
  Profile = -> Sketch003
  ReferenceAxis = -> Sketch003 [N_Axis]
  Type = 0
  expr: Length = Spreadsheet.dim_text_h
FEATURE [PartDesign::Pad] Pad003  label="YearPad"
  BaseFeature = -> Pad002
  Direction = (0,0,1)
  Length = 2
  Length2 = 10
  Profile = -> Sketch004
  ReferenceAxis = -> Sketch004 [N_Axis]
  Type = 0
  expr: Length = Spreadsheet.dim_text_h
FEATURE [PartDesign::Body] Body
  Group = -> [DatumPlane,Sketch001,Pad,Sketch002,Sketch003,Sketch004,Pad001,Pad002,Pad003]
  Origin = -> Origin
  Tip = -> Pad003
FEATURE [Mesh::Feature] Mesh  label="Body (Meshed)"
